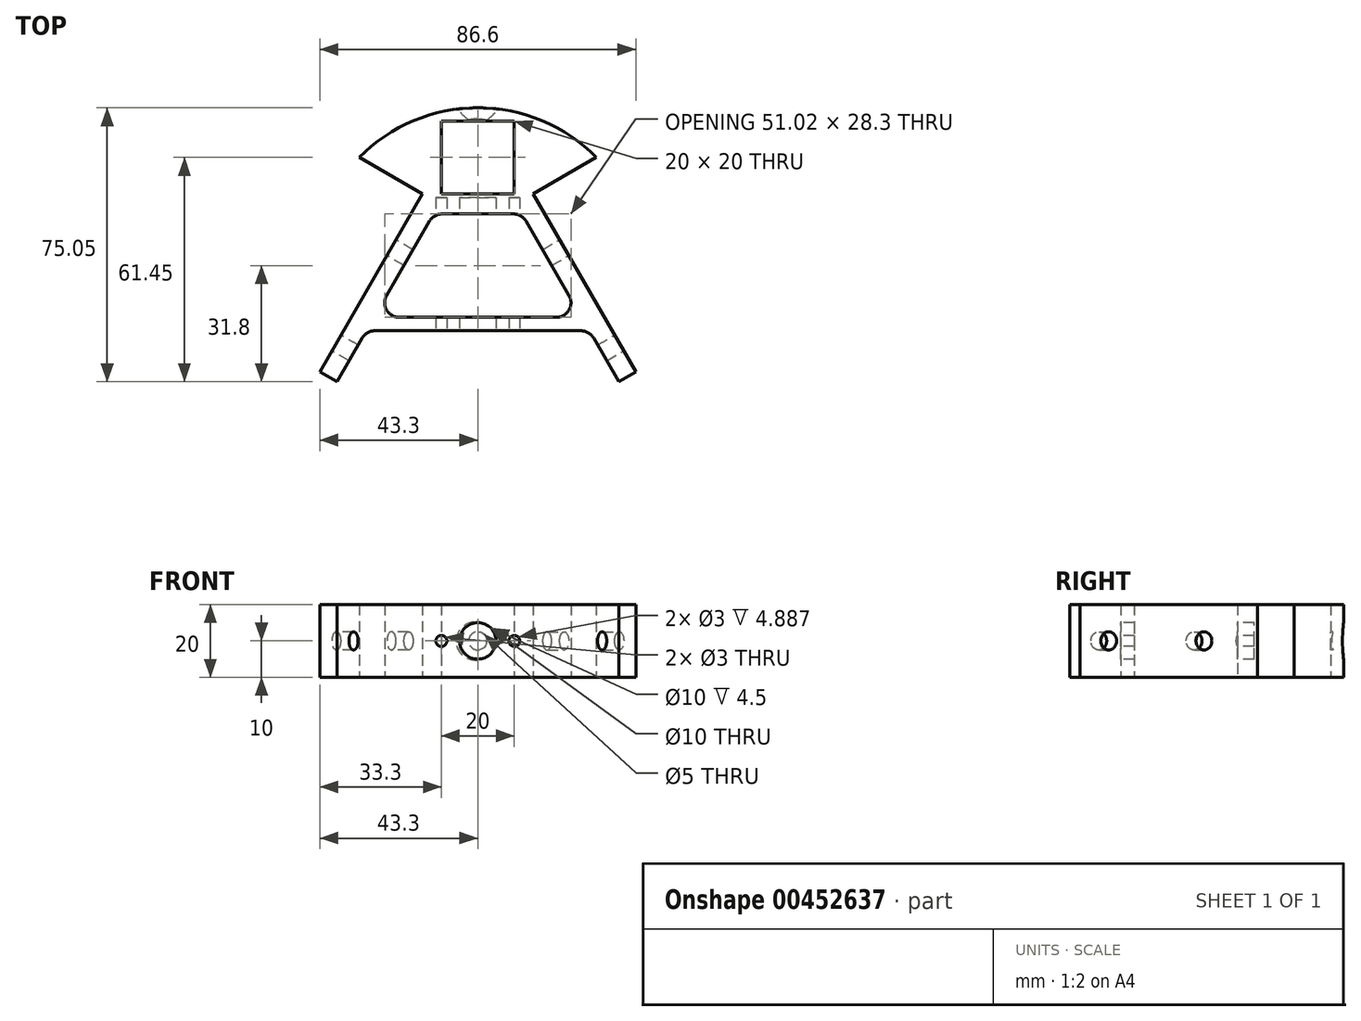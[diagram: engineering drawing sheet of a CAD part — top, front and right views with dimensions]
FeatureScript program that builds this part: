
annotation { "Feature Type Name" : "Feature", "Feature Type Description" : "" }
export const myFeature = defineFeature(function(context is Context, id is Id, definition is map)
    precondition{}
    {
        {
            var Q0;
            Q0=qCreatedBy(makeId("Top.planeOp"),FACE);
            var sketch = newSketch(context, id + "F0", { "sketchPlane" : qUnion([Q0])});
            skLineSegment(sketch, "E0", {"start": v(0, 0) * mm, "end": v(0, -10) * mm, "construction": true});
            skLineSegment(sketch, "E1.bottom", {"start": v(10, -10) * mm, "end": v(0, -10) * mm});
            skLineSegment(sketch, "E1.top", {"start": v(10, 10) * mm, "end": v(0, 10) * mm});
            skLineSegment(sketch, "E1.left", {"start": v(10, -10) * mm, "end": v(10, 10) * mm});
            skPoint(sketch, "E1.middle", {"position": v(0, 0) * mm});
            skLineSegment(sketch, "E2", {"start": v(0, 0) * mm, "end": v(0, 10) * mm, "construction": true});
            skPoint(sketch, "E1.right.start.orphan", {"position": v(-10, -10) * mm});
            skPoint(sketch, "E3.orphan", {"position": v(-10, 10) * mm});
            skLineSegment(sketch, "E4", {"start": v(0, -10) * mm, "end": v(0, -72.74) * mm, "construction": true});
            skLineSegment(sketch, "E5", {"start": v(15.16, -10) * mm, "end": v(43.3, -58.75) * mm});
            skLineSegment(sketch, "E6", {"start": v(43.3, -58.75) * mm, "end": v(60.63, -48.75) * mm, "construction": true});
            skLineSegment(sketch, "E7", {"start": v(60.63, -48.75) * mm, "end": v(32.48, 0) * mm, "construction": true});
            skLineSegment(sketch, "E8", {"start": v(0, 10) * mm, "end": v(0, 13.6) * mm});
            skLineSegment(sketch, "E9", {"start": v(0, 13.6) * mm, "end": v(-73.6, 13.6) * mm, "construction": true});
            skLineSegment(sketch, "E10", {"start": v(43.3, -58.75) * mm, "end": v(38.63, -61.45) * mm});
            skLineSegment(sketch, "E11", {"start": v(0, -10) * mm, "end": v(0, -10) * mm});
            skArc(sketch, "E12", {"start": v(0, 13.6) * mm, "mid": v(17.6, 10.06) * mm, "end": v(32.48, 0) * mm});
            skLineSegment(sketch, "E13", {"start": v(15.16, -10) * mm, "end": v(32.48, 0) * mm});
            skLineSegment(sketch, "E14", {"start": v(38.63, -61.45) * mm, "end": v(31.73, -49.5) * mm});
            skLineSegment(sketch, "E15", {"start": v(28.27, -47.5) * mm, "end": v(0, -47.5) * mm});
            skLineSegment(sketch, "E16", {"start": v(0, -47.5) * mm, "end": v(0, -43.8) * mm});
            skLineSegment(sketch, "E17", {"start": v(0, -43.8) * mm, "end": v(21.51, -43.8) * mm});
            skLineSegment(sketch, "E18", {"start": v(24.97, -37.8) * mm, "end": v(13.25, -17.5) * mm});
            skLineSegment(sketch, "E19", {"start": v(9.8, -15.5) * mm, "end": v(0, -15.5) * mm});
            skLineSegment(sketch, "E20", {"start": v(0, -15.5) * mm, "end": v(0, -10) * mm});
            skPoint(sketch, "E21.visualSharp", {"position": v(12.1, -15.5) * mm});
            skArc(sketch, "E21.filletArc", {"start": v(13.25, -17.5) * mm, "mid": v(11.8, -16.04) * mm, "end": v(9.8, -15.5) * mm});
            skPoint(sketch, "E22.visualSharp", {"position": v(28.44, -43.8) * mm});
            skArc(sketch, "E22.filletArc", {"start": v(21.51, -43.8) * mm, "mid": v(24.97, -41.8) * mm, "end": v(24.97, -37.8) * mm});
            skPoint(sketch, "E23.visualSharp", {"position": v(30.57, -47.5) * mm});
            skArc(sketch, "E23.filletArc", {"start": v(31.73, -49.5) * mm, "mid": v(30.27, -48.04) * mm, "end": v(28.27, -47.5) * mm});
            skSolve(sketch);
        }
        {
            var Q0;
            Q0=qSketchRegion(id+"F0",true);
            extrude(context, id + "F1", {"entities" : qUnion([Q0]), "depth" : 20 * mm});
        }
        {
            var Q0;
            Q0=makeQuery(id+"F1.opExtrude","SWEPT_FACE",FACE,{"disambiguationData":[OSD([sQuery(id+"F0.wireOp",EDGE,"E5")])]});
            var sketch = newSketch(context, id + "F2", { "sketchPlane" : qUnion([Q0])});
            skCircle(sketch, "E24", {"center": v(-63.4, 10) * mm, "radius": 2.5 * mm});
            skCircle(sketch, "E25", {"center": v(-33.25, 10) * mm, "radius": 2.5 * mm});
            skLineSegment(sketch, "E26", {"start": v(-33.25, 10) * mm, "end": v(-63.4, 10) * mm, "construction": true});
            skLineSegment(sketch, "E27", {"start": v(-72.53, 10) * mm, "end": v(-63.4, 10) * mm, "construction": true});
            skSolve(sketch);
        }
        {
            var Q0;
            Q0=qSketchRegion(id+"F2",true);
            extrude(context, id + "F3", {"entities" : qUnion([Q0]), "operationType" : NewBodyOperationType.REMOVE, "oppositeDirection" : true, "depth" : 25 * mm});
        }
        {
            var Q0;
            Q0=makeQuery(id+"F1.opExtrude","SWEPT_FACE",FACE,{"disambiguationData":[OSD([sQuery(id+"F0.wireOp",EDGE,"E15")])]});
            var sketch = newSketch(context, id + "F4", { "sketchPlane" : qUnion([Q0])});
            skCircle(sketch, "E28", {"center": v(0, 10) * mm, "radius": 5 * mm});
            skCircle(sketch, "E29", {"center": v(10, 10) * mm, "radius": 1.5 * mm});
            skLineSegment(sketch, "E30", {"start": v(0, 10) * mm, "end": v(10, 10) * mm, "construction": true});
            skSolve(sketch);
        }
        {
            var Q0;
            Q0=qSketchRegion(id+"F4",true);
            extrude(context, id + "F5", {"entities" : qUnion([Q0]), "operationType" : NewBodyOperationType.REMOVE, "oppositeDirection" : true, "depth" : 36.5 * mm});
        }
        {
            var Q0;
            Q0=makeQuery(id+"F1.opExtrude","SWEPT_FACE",FACE,{"disambiguationData":[OSD([sQuery(id+"F0.wireOp",EDGE,"E1.top")])]});
            var sketch = newSketch(context, id + "F6", { "sketchPlane" : qUnion([Q0])});
            skCircle(sketch, "E31", {"center": v(0, 10) * mm, "radius": 2.5 * mm});
            skSolve(sketch);
        }
        {
            var Q0;
            {var subQ0=sQuery(id+"F6.wireOp",EDGE,"E31");var subQ1=makeQuery(id+"F1.opExtrude","SWEPT_EDGE",EDGE,{"disambiguationData":[OSD([sQuery(id+"F0.wireOp",EDGE,"E1.top"),sQuery(id+"F0.wireOp",EDGE,"E8")])]});var subQ2=makeQuery(id+"F6.imprint","INTERSECT",VERTEX,{"disambiguationData":[OD(0.0)],"derivedFrom":[subQ1,subQ0]});Q0=makeQuery(id+"F6.imprint","IMPRINT",FACE,{"disambiguationData":[TD([[makeQuery(id+"F6.imprint","IMPRINT",EDGE,{"disambiguationData":[TD([[subQ2,1.0]])],"derivedFrom":subQ0}),1.0]])]});}
            var Q1;
            {var subQ0=sQuery(id+"F6.wireOp",EDGE,"E31");var subQ1=makeQuery(id+"F1.opExtrude","SWEPT_EDGE",EDGE,{"disambiguationData":[OSD([sQuery(id+"F0.wireOp",EDGE,"E1.top"),sQuery(id+"F0.wireOp",EDGE,"E8")])]});var subQ2=makeQuery(id+"F6.imprint","INTERSECT",VERTEX,{"disambiguationData":[OD(0.0)],"derivedFrom":[subQ1,subQ0]});Q1=makeQuery(id+"F6.imprint","IMPRINT",FACE,{"disambiguationData":[TD([[makeQuery(id+"F6.imprint","IMPRINT",EDGE,{"disambiguationData":[TD([[subQ2,-1.0]])],"derivedFrom":subQ0}),1.0]])]});}
            extrude(context, id + "F7", {"entities" : qUnion([Q0, Q1]), "operationType" : NewBodyOperationType.REMOVE, "oppositeDirection" : true, "depth" : 25 * mm});
        }
        {
            var Q0;
            Q0=makeQuery(id+"F7.boolean.opBoolean","INTERSECT",EDGE,{"derivedFrom":[makeQuery(id+"F1.opExtrude","SWEPT_FACE",FACE,{"disambiguationData":[OSD([sQuery(id+"F0.wireOp",EDGE,"E12")])]}),makeQuery(id+"F7.opExtrude","SWEPT_FACE",FACE,{"disambiguationData":[OSD([sQuery(id+"F6.wireOp",EDGE,"E31")])]})]});
            chamfer(context, id + "F8", {"entities" : qUnion([Q0]), "width" : 3 * mm, "tangentPropagation" : true});
        }
        {
            var Q0;
            Q0=makeQuery(id+"F1.opExtrude","SWEPT_BODY",BODY,{"disambiguationData":[OSD([sQuery(id+"F0.wireOp",EDGE,"E1.bottom"),sQuery(id+"F0.wireOp",EDGE,"E1.top"),sQuery(id+"F0.wireOp",EDGE,"E1.left"),sQuery(id+"F0.wireOp",EDGE,"E5"),sQuery(id+"F0.wireOp",EDGE,"E8"),sQuery(id+"F0.wireOp",EDGE,"E10"),sQuery(id+"F0.wireOp",EDGE,"E12"),sQuery(id+"F0.wireOp",EDGE,"E13"),sQuery(id+"F0.wireOp",EDGE,"E14"),sQuery(id+"F0.wireOp",EDGE,"E15"),sQuery(id+"F0.wireOp",EDGE,"E16"),sQuery(id+"F0.wireOp",EDGE,"E17"),sQuery(id+"F0.wireOp",EDGE,"E18"),sQuery(id+"F0.wireOp",EDGE,"E19"),sQuery(id+"F0.wireOp",EDGE,"E20"),sQuery(id+"F0.wireOp",EDGE,"E21.filletArc"),sQuery(id+"F0.wireOp",EDGE,"E22.filletArc"),sQuery(id+"F0.wireOp",EDGE,"E23.filletArc")])]});
            var Q1;
            Q1=qCreatedBy(makeId("Right.planeOp"),FACE);
            mirror(context, id + "F9", {"operationType" : NewBodyOperationType.ADD, "entities" : qUnion([Q0]), "mirrorPlane" : qUnion([Q1])});
        }
    });
